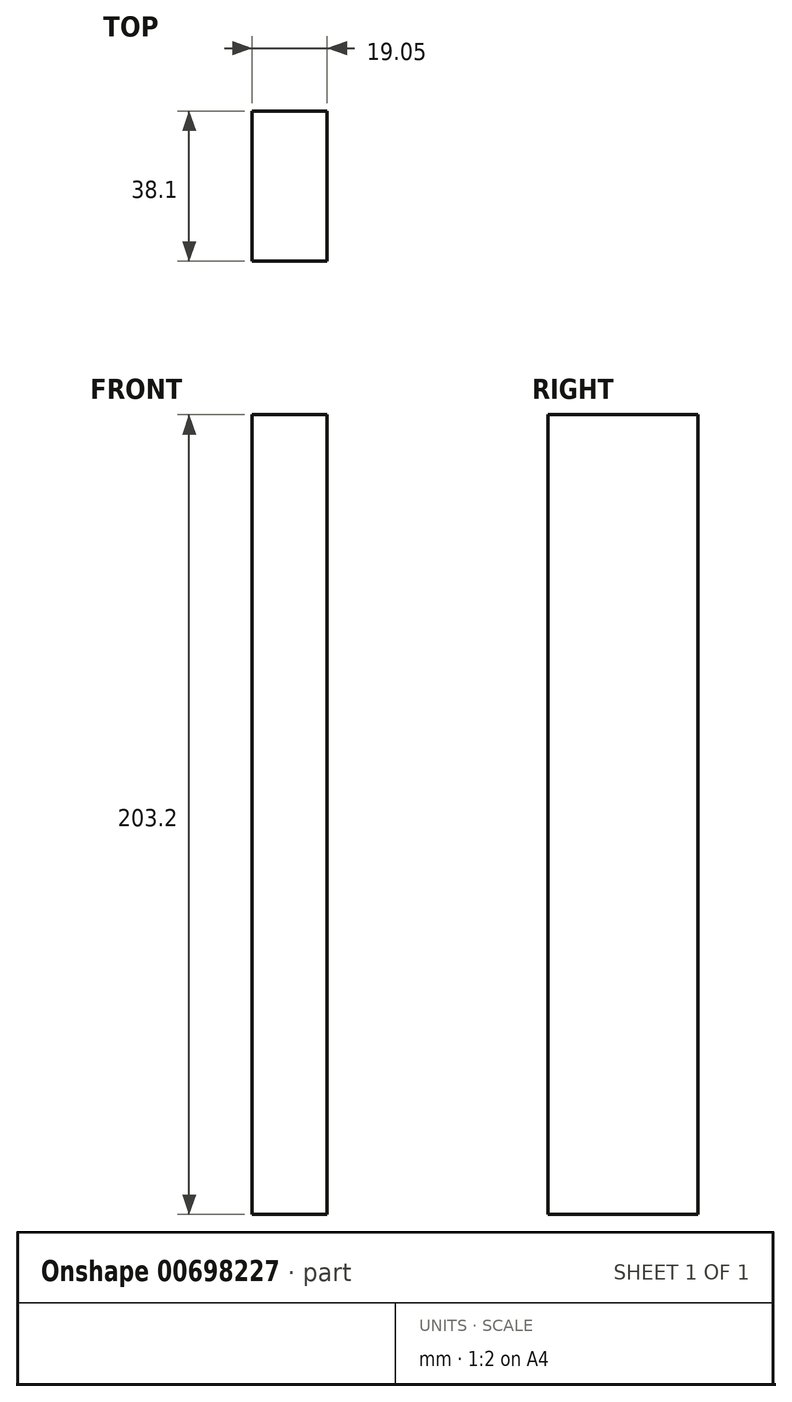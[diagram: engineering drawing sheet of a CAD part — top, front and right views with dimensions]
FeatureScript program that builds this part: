
annotation { "Feature Type Name" : "Feature", "Feature Type Description" : "" }
export const myFeature = defineFeature(function(context is Context, id is Id, definition is map)
    precondition{}
    {
        {
            var Q0;
            Q0=qCreatedBy(makeId("Front.planeOp"),FACE);
            var sketch = newSketch(context, id + "F0", { "sketchPlane" : qUnion([Q0])});
            skLineSegment(sketch, "E0.bottom", {"start": v(-114.4, 205.07) * mm, "end": v(-95.35, 205.07) * mm});
            skLineSegment(sketch, "E0.top", {"start": v(-114.4, 1.87) * mm, "end": v(-95.35, 1.87) * mm});
            skLineSegment(sketch, "E0.left", {"start": v(-114.4, 205.07) * mm, "end": v(-114.4, 1.87) * mm});
            skLineSegment(sketch, "E0.right", {"start": v(-95.35, 205.07) * mm, "end": v(-95.35, 1.87) * mm});
            skSolve(sketch);
        }
        {
            var Q0;
            Q0=makeQuery(id+"F0.imprint","IMPRINT",FACE,{"disambiguationData":[TD([[makeQuery(id+"F0.imprint","IMPRINT",EDGE,{"derivedFrom":sQuery(id+"F0.wireOp",EDGE,"E0.bottom")}),-1.0]])]});
            extrude(context, id + "F1", {"entities" : qUnion([Q0]), "depth" : 38.1 * mm, "offsetDistance" : 25.4 * mm});
        }
    });
